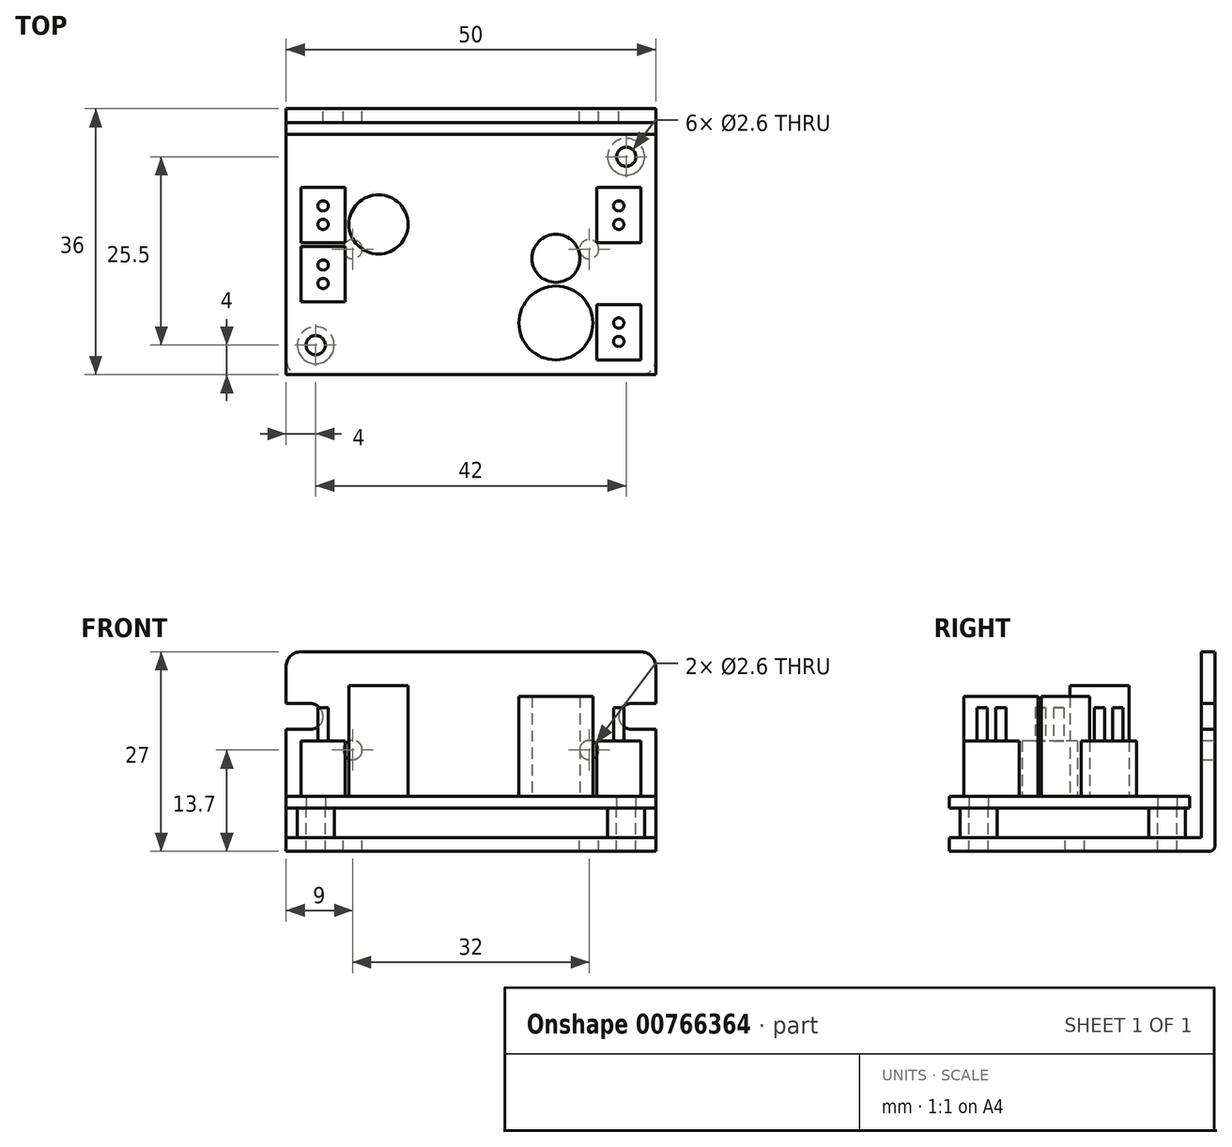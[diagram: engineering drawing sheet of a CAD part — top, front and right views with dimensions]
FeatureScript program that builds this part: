
annotation { "Feature Type Name" : "Feature", "Feature Type Description" : "" }
export const myFeature = defineFeature(function(context is Context, id is Id, definition is map)
    precondition{}
    {
        {
            var Q0;
            Q0=qCreatedBy(makeId("Right.planeOp"),FACE);
            var sketch = newSketch(context, id + "F0", { "sketchPlane" : qUnion([Q0])});
            skLineSegment(sketch, "E0", {"start": v(-17.6, 0) * mm, "end": v(17.6, 0) * mm});
            skLineSegment(sketch, "E1", {"start": v(18.4, 0.8) * mm, "end": v(18.4, 27) * mm});
            skLineSegment(sketch, "E2", {"start": v(18.4, 27) * mm, "end": v(16.55, 27) * mm});
            skLineSegment(sketch, "E3", {"start": v(16.55, 27) * mm, "end": v(16.55, 1.85) * mm});
            skLineSegment(sketch, "E4", {"start": v(16.55, 1.85) * mm, "end": v(-17.6, 1.85) * mm});
            skLineSegment(sketch, "E5", {"start": v(-17.6, 1.85) * mm, "end": v(-17.6, 0) * mm});
            skPoint(sketch, "E6.visualSharp", {"position": v(18.4, 0) * mm});
            skArc(sketch, "E6.filletArc", {"start": v(17.6, 0) * mm, "mid": v(18.17, 0.23) * mm, "end": v(18.4, 0.8) * mm});
            skSolve(sketch);
        }
        {
            var Q0;
            Q0=makeQuery(id+"F0.imprint","IMPRINT",FACE,{"disambiguationData":[TD([[makeQuery(id+"F0.imprint","IMPRINT",EDGE,{"derivedFrom":sQuery(id+"F0.wireOp",EDGE,"E0")}),1.0]])]});
            extrude(context, id + "F1", {"entities" : qUnion([Q0]), "endBound" : BoundingType.SYMMETRIC, "depth" : 50 * mm, "offsetDistance" : 25 * mm});
        }
        {
            var Q0;
            Q0=makeQuery(id+"F1.opExtrude","SWEPT_FACE",FACE,{"disambiguationData":[OSD([sQuery(id+"F0.wireOp",EDGE,"E4")])]});
            var sketch = newSketch(context, id + "F2", { "sketchPlane" : qUnion([Q0])});
            skCircle(sketch, "E7", {"center": v(21, 11.9) * mm, "radius": 1.3 * mm});
            skCircle(sketch, "E8", {"center": v(-21, -13.6) * mm, "radius": 1.3 * mm});
            skCircle(sketch, "E9", {"center": v(-16, -0.6) * mm, "radius": 1.3 * mm});
            skCircle(sketch, "E10", {"center": v(16, -0.6) * mm, "radius": 1.3 * mm});
            skCircle(sketch, "E11", {"center": v(21, 11.9) * mm, "radius": 2.5 * mm});
            skCircle(sketch, "E12", {"center": v(-21, -13.6) * mm, "radius": 2.5 * mm});
            skSolve(sketch);
        }
        {
            var Q0;
            Q0=makeQuery(id+"F2.imprint","IMPRINT",FACE,{"disambiguationData":[TD([[makeQuery(id+"F2.imprint","IMPRINT",EDGE,{"derivedFrom":sQuery(id+"F2.wireOp",EDGE,"E8")}),1.0]])]});
            var Q1;
            Q1=makeQuery(id+"F2.imprint","IMPRINT",FACE,{"disambiguationData":[TD([[makeQuery(id+"F2.imprint","IMPRINT",EDGE,{"derivedFrom":sQuery(id+"F2.wireOp",EDGE,"E9")}),1.0]])]});
            var Q2;
            Q2=makeQuery(id+"F2.imprint","IMPRINT",FACE,{"disambiguationData":[TD([[makeQuery(id+"F2.imprint","IMPRINT",EDGE,{"derivedFrom":sQuery(id+"F2.wireOp",EDGE,"E7")}),1.0]])]});
            var Q3;
            Q3=makeQuery(id+"F2.imprint","IMPRINT",FACE,{"disambiguationData":[TD([[makeQuery(id+"F2.imprint","IMPRINT",EDGE,{"derivedFrom":sQuery(id+"F2.wireOp",EDGE,"E10")}),1.0]])]});
            extrude(context, id + "F3", {"entities" : qUnion([Q0, Q1, Q2, Q3]), "operationType" : NewBodyOperationType.REMOVE, "endBound" : BoundingType.THROUGH_ALL, "oppositeDirection" : true, "depth" : 25 * mm, "offsetDistance" : 25 * mm});
        }
        {
            var Q0;
            Q0=makeQuery(id+"F2.imprint","IMPRINT",FACE,{"disambiguationData":[TD([[makeQuery(id+"F2.imprint","IMPRINT",EDGE,{"derivedFrom":sQuery(id+"F2.wireOp",EDGE,"E8")}),-1.0]])]});
            var Q1;
            Q1=makeQuery(id+"F2.imprint","IMPRINT",FACE,{"disambiguationData":[TD([[makeQuery(id+"F2.imprint","IMPRINT",EDGE,{"derivedFrom":sQuery(id+"F2.wireOp",EDGE,"E7")}),-1.0]])]});
            extrude(context, id + "F4", {"entities" : qUnion([Q0, Q1]), "operationType" : NewBodyOperationType.ADD, "depth" : 4 * mm, "offsetDistance" : 25 * mm});
        }
        {
            var Q0;
            Q0=makeQuery(id+"F1.opExtrude","SWEPT_FACE",FACE,{"disambiguationData":[OSD([sQuery(id+"F0.wireOp",EDGE,"E1")])]});
            var sketch = newSketch(context, id + "F5", { "sketchPlane" : qUnion([Q0])});
            skCircle(sketch, "E13", {"center": v(-16, 13.7) * mm, "radius": 1.3 * mm});
            skCircle(sketch, "E14", {"center": v(16, 13.7) * mm, "radius": 1.3 * mm});
            skCircle(sketch, "E15", {"center": v(-21.75, 18.25) * mm, "radius": 1.75 * mm});
            skCircle(sketch, "E16", {"center": v(21.75, 18.25) * mm, "radius": 1.75 * mm});
            skLineSegment(sketch, "E17", {"start": v(0, 27) * mm, "end": v(0, 0) * mm, "construction": true});
            skLineSegment(sketch, "E18", {"start": v(-21.75, 20) * mm, "end": v(-25, 20) * mm});
            skLineSegment(sketch, "E19", {"start": v(-21.75, 16.5) * mm, "end": v(-25, 16.5) * mm});
            skLineSegment(sketch, "E20.MirrorCS", {"start": v(21.75, 20) * mm, "end": v(25, 20) * mm});
            skLineSegment(sketch, "E21.MirrorCS", {"start": v(21.75, 16.5) * mm, "end": v(25, 16.5) * mm});
            skSolve(sketch);
        }
        {
            var Q0;
            Q0=makeQuery(id+"F5.imprint","IMPRINT",FACE,{"disambiguationData":[TD([[makeQuery(id+"F5.imprint","IMPRINT",EDGE,{"derivedFrom":sQuery(id+"F5.wireOp",EDGE,"E13")}),1.0]])]});
            var Q1;
            Q1=makeQuery(id+"F5.imprint","IMPRINT",FACE,{"disambiguationData":[TD([[makeQuery(id+"F5.imprint","IMPRINT",EDGE,{"derivedFrom":sQuery(id+"F5.wireOp",EDGE,"E14")}),1.0]])]});
            var Q2;
            {var subQ0=sQuery(id+"F5.wireOp",EDGE,"E20.MirrorCS");Q2=makeQuery(id+"F5.imprint","IMPRINT",FACE,{"disambiguationData":[TD([[makeQuery(id+"F5.imprint","IMPRINT",EDGE,{"derivedFrom":subQ0}),-1.0]])]});}
            var Q3;
            {var subQ0=sQuery(id+"F5.wireOp",EDGE,"E16");var subQ1=makeQuery(id+"F5.imprint","INTERSECT",VERTEX,{"derivedFrom":[subQ0,sQuery(id+"F5.wireOp",EDGE,"E20.MirrorCS")]});Q3=makeQuery(id+"F5.imprint","IMPRINT",FACE,{"disambiguationData":[TD([[makeQuery(id+"F5.imprint","IMPRINT",EDGE,{"disambiguationData":[TD([[subQ1,-1.0]])],"derivedFrom":subQ0}),1.0]])]});}
            var Q4;
            {var subQ0=sQuery(id+"F5.wireOp",EDGE,"E18");Q4=makeQuery(id+"F5.imprint","IMPRINT",FACE,{"disambiguationData":[TD([[makeQuery(id+"F5.imprint","IMPRINT",EDGE,{"derivedFrom":subQ0}),1.0]])]});}
            var Q5;
            {var subQ0=sQuery(id+"F5.wireOp",EDGE,"E15");var subQ1=makeQuery(id+"F5.imprint","INTERSECT",VERTEX,{"derivedFrom":[subQ0,sQuery(id+"F5.wireOp",EDGE,"E18")]});Q5=makeQuery(id+"F5.imprint","IMPRINT",FACE,{"disambiguationData":[TD([[makeQuery(id+"F5.imprint","IMPRINT",EDGE,{"disambiguationData":[TD([[subQ1,-1.0]])],"derivedFrom":subQ0}),1.0]])]});}
            extrude(context, id + "F6", {"entities" : qUnion([Q0, Q1, Q2, Q3, Q4, Q5]), "operationType" : NewBodyOperationType.REMOVE, "endBound" : BoundingType.THROUGH_ALL, "oppositeDirection" : true, "depth" : 25 * mm, "offsetDistance" : 25 * mm});
        }
        {
            var Q0;
            Q0=makeQuery(id+"F1.opExtrude","CAP_EDGE",EDGE,{"disambiguationData":[OSD([sQuery(id+"F0.wireOp",EDGE,"E5")])],"isStart":false});
            var Q1;
            Q1=makeQuery(id+"F1.opExtrude","CAP_EDGE",EDGE,{"disambiguationData":[OSD([sQuery(id+"F0.wireOp",EDGE,"E5")])],"isStart":true});
            var Q2;
            Q2=makeQuery(id+"F1.opExtrude","CAP_EDGE",EDGE,{"disambiguationData":[OSD([sQuery(id+"F0.wireOp",EDGE,"E2")])],"isStart":true});
            var Q3;
            Q3=makeQuery(id+"F1.opExtrude","CAP_EDGE",EDGE,{"disambiguationData":[OSD([sQuery(id+"F0.wireOp",EDGE,"E2")])],"isStart":false});
            fillet(context, id + "F7", {"entities" : qUnion([Q0, Q1, Q2, Q3]), "tangentPropagation" : true, "radius" : 2 * mm, "defaultsChanged" : true, "vertexSettings" : [], "allowEdgeOverflow" : false});
        }
        {
            var Q0;
            Q0=makeQuery(id+"F4.opExtrude","CAP_FACE",FACE,{"disambiguationData":[OSD([sQuery(id+"F2.wireOp",EDGE,"E8"),sQuery(id+"F2.wireOp",EDGE,"E12")])],"isStart":false});
            var sketch = newSketch(context, id + "F8", { "sketchPlane" : qUnion([Q0])});
            skLineSegment(sketch, "E22.bottom", {"start": v(-25, -17.6) * mm, "end": v(25, -17.6) * mm});
            skLineSegment(sketch, "E22.top", {"start": v(-25, 14.95) * mm, "end": v(25, 14.95) * mm});
            skLineSegment(sketch, "E22.left", {"start": v(-25, -17.6) * mm, "end": v(-25, 14.95) * mm});
            skLineSegment(sketch, "E22.right", {"start": v(25, -17.6) * mm, "end": v(25, 14.95) * mm});
            skPoint(sketch, "E23.0", {"position": v(-25, 0.47) * mm});
            skPoint(sketch, "E24.0", {"position": v(0, -17.6) * mm});
            skPoint(sketch, "E25.0", {"position": v(25, 0.47) * mm});
            skCircle(sketch, "E26.0", {"center": v(21, 11.9) * mm, "radius": 1.3 * mm});
            skSolve(sketch);
        }
        {
            var Q0;
            Q0=makeQuery(id+"F8.imprint","IMPRINT",FACE,{"disambiguationData":[TD([[makeQuery(id+"F8.imprint","IMPRINT",EDGE,{"derivedFrom":sQuery(id+"F8.wireOp",EDGE,"E22.bottom")}),1.0]])]});
            var Q1;
            Q1=makeQuery(id+"F8.imprint","IMPRINT",FACE,{"disambiguationData":[TD([[makeQuery(id+"F8.imprint","IMPRINT",EDGE,{"derivedFrom":makeQuery(id+"F4.opExtrude","CAP_EDGE",EDGE,{"disambiguationData":[OSD([sQuery(id+"F2.wireOp",EDGE,"E8")])],"isStart":false})}),-1.0]])]});
            extrude(context, id + "F9", {"entities" : qUnion([Q0, Q1]), "depth" : 1.6 * mm, "offsetDistance" : 25 * mm});
        }
        {
            var Q0;
            Q0=makeQuery(id+"F9.opExtrude","CAP_FACE",FACE,{"disambiguationData":[OSD([sQuery(id+"F2.wireOp",EDGE,"E8"),sQuery(id+"F8.wireOp",EDGE,"E22.bottom"),sQuery(id+"F8.wireOp",EDGE,"E22.top"),sQuery(id+"F8.wireOp",EDGE,"E22.left"),sQuery(id+"F8.wireOp",EDGE,"E22.right"),sQuery(id+"F8.wireOp",EDGE,"E26.0")])],"isStart":false});
            var sketch = newSketch(context, id + "F10", { "sketchPlane" : qUnion([Q0])});
            skLineSegment(sketch, "E27.0", {"start": v(-23, 12.95) * mm, "end": v(23, 12.95) * mm, "construction": true});
            skLineSegment(sketch, "E27.1", {"start": v(-23, -15.6) * mm, "end": v(-23, 12.95) * mm, "construction": true});
            skLineSegment(sketch, "E27.2", {"start": v(-23, -15.6) * mm, "end": v(23, -15.6) * mm, "construction": true});
            skLineSegment(sketch, "E27.3", {"start": v(23, -15.6) * mm, "end": v(23, 12.95) * mm, "construction": true});
            skLineSegment(sketch, "E28.bottom", {"start": v(-23, 7.75) * mm, "end": v(-17, 7.75) * mm});
            skLineSegment(sketch, "E28.top", {"start": v(-23, 0.25) * mm, "end": v(-17, 0.25) * mm});
            skLineSegment(sketch, "E28.left", {"start": v(-23, 7.75) * mm, "end": v(-23, 0.25) * mm});
            skLineSegment(sketch, "E28.right", {"start": v(-17, 7.75) * mm, "end": v(-17, 0.25) * mm});
            skLineSegment(sketch, "E29.bottom", {"start": v(-23, -0.25) * mm, "end": v(-17, -0.25) * mm});
            skLineSegment(sketch, "E29.top", {"start": v(-23, -7.75) * mm, "end": v(-17, -7.75) * mm});
            skLineSegment(sketch, "E29.left", {"start": v(-23, -0.25) * mm, "end": v(-23, -7.75) * mm});
            skLineSegment(sketch, "E29.right", {"start": v(-17, -0.25) * mm, "end": v(-17, -7.75) * mm});
            skLineSegment(sketch, "E30.bottom", {"start": v(23, -8.1) * mm, "end": v(17, -8.1) * mm});
            skLineSegment(sketch, "E30.top", {"start": v(23, -15.6) * mm, "end": v(17, -15.6) * mm});
            skLineSegment(sketch, "E30.left", {"start": v(23, -8.1) * mm, "end": v(23, -15.6) * mm});
            skLineSegment(sketch, "E30.right", {"start": v(17, -8.1) * mm, "end": v(17, -15.6) * mm});
            skLineSegment(sketch, "E31.bottom", {"start": v(23, 7.75) * mm, "end": v(17, 7.75) * mm});
            skLineSegment(sketch, "E31.top", {"start": v(23, 0.25) * mm, "end": v(17, 0.25) * mm});
            skLineSegment(sketch, "E31.left", {"start": v(23, 7.75) * mm, "end": v(23, 0.25) * mm});
            skLineSegment(sketch, "E31.right", {"start": v(17, 7.75) * mm, "end": v(17, 0.25) * mm});
            skLineSegment(sketch, "E32", {"start": v(-20, 0.25) * mm, "end": v(-20, -0.25) * mm, "construction": true});
            skPoint(sketch, "E33", {"position": v(-20, 0) * mm});
            skCircle(sketch, "E34", {"center": v(11.5, -10.6) * mm, "radius": 5 * mm});
            skCircle(sketch, "E35", {"center": v(11.5, -1.85) * mm, "radius": 3.25 * mm});
            skCircle(sketch, "E36", {"center": v(-12.5, 2.75) * mm, "radius": 4 * mm});
            skLineSegment(sketch, "E37.bottom", {"start": v(-8, 3.25) * mm, "end": v(1.5, 3.25) * mm});
            skLineSegment(sketch, "E37.top", {"start": v(-8, -1.25) * mm, "end": v(1.5, -1.25) * mm});
            skLineSegment(sketch, "E37.left", {"start": v(-8, 3.25) * mm, "end": v(-8, -1.25) * mm});
            skLineSegment(sketch, "E37.right", {"start": v(1.5, 3.25) * mm, "end": v(1.5, -1.25) * mm});
            skLineSegment(sketch, "E38", {"start": v(-8, -1.25) * mm, "end": v(-17, -1.25) * mm, "construction": true});
            skSolve(sketch);
        }
        {
            var Q0;
            Q0=makeQuery(id+"F10.imprint","IMPRINT",FACE,{"disambiguationData":[TD([[makeQuery(id+"F10.imprint","IMPRINT",EDGE,{"derivedFrom":sQuery(id+"F10.wireOp",EDGE,"E28.bottom")}),-1.0]])]});
            var Q1;
            Q1=makeQuery(id+"F10.imprint","IMPRINT",FACE,{"disambiguationData":[TD([[makeQuery(id+"F10.imprint","IMPRINT",EDGE,{"derivedFrom":sQuery(id+"F10.wireOp",EDGE,"E29.bottom")}),-1.0]])]});
            var Q2;
            Q2=makeQuery(id+"F10.imprint","IMPRINT",FACE,{"disambiguationData":[TD([[makeQuery(id+"F10.imprint","IMPRINT",EDGE,{"derivedFrom":sQuery(id+"F10.wireOp",EDGE,"E30.bottom")}),1.0]])]});
            var Q3;
            Q3=makeQuery(id+"F10.imprint","IMPRINT",FACE,{"disambiguationData":[TD([[makeQuery(id+"F10.imprint","IMPRINT",EDGE,{"derivedFrom":sQuery(id+"F10.wireOp",EDGE,"E31.bottom")}),1.0]])]});
            extrude(context, id + "F11", {"entities" : qUnion([Q0, Q1, Q2, Q3]), "depth" : 7.5 * mm, "offsetDistance" : 25 * mm});
        }
        {
            var Q0;
            Q0=makeQuery(id+"F10.imprint","IMPRINT",FACE,{"disambiguationData":[TD([[makeQuery(id+"F10.imprint","IMPRINT",EDGE,{"derivedFrom":sQuery(id+"F10.wireOp",EDGE,"E34")}),1.0]])]});
            var Q1;
            Q1=makeQuery(id+"F10.imprint","IMPRINT",FACE,{"disambiguationData":[TD([[makeQuery(id+"F10.imprint","IMPRINT",EDGE,{"derivedFrom":sQuery(id+"F10.wireOp",EDGE,"E35")}),1.0]])]});
            extrude(context, id + "F12", {"entities" : qUnion([Q0, Q1]), "depth" : 13.5 * mm, "offsetDistance" : 25 * mm});
        }
        {
            var Q0;
            Q0=makeQuery(id+"F10.imprint","IMPRINT",FACE,{"disambiguationData":[TD([[makeQuery(id+"F10.imprint","IMPRINT",EDGE,{"derivedFrom":sQuery(id+"F10.wireOp",EDGE,"E36")}),1.0]])]});
            extrude(context, id + "F13", {"entities" : qUnion([Q0]), "depth" : 15 * mm, "offsetDistance" : 25 * mm});
        }
        {
            var Q0;
            Q0=makeQuery(id+"F11.opExtrude","CAP_FACE",FACE,{"disambiguationData":[OSD([sQuery(id+"F10.wireOp",EDGE,"E30.bottom"),sQuery(id+"F10.wireOp",EDGE,"E30.top"),sQuery(id+"F10.wireOp",EDGE,"E30.left"),sQuery(id+"F10.wireOp",EDGE,"E30.right")])],"isStart":false});
            var sketch = newSketch(context, id + "F14", { "sketchPlane" : qUnion([Q0])});
            skLineSegment(sketch, "E39", {"start": v(17, -11.85) * mm, "end": v(23, -11.85) * mm, "construction": true});
            skLineSegment(sketch, "E40.0.0", {"start": v(17, 0.25) * mm, "end": v(23, 0.25) * mm, "construction": true});
            skLineSegment(sketch, "E40.0.1", {"start": v(23, 0.25) * mm, "end": v(23, 7.75) * mm, "construction": true});
            skLineSegment(sketch, "E40.0.2", {"start": v(23, 7.75) * mm, "end": v(17, 7.75) * mm, "construction": true});
            skLineSegment(sketch, "E40.0.3", {"start": v(17, 7.75) * mm, "end": v(17, 0.25) * mm, "construction": true});
            skLineSegment(sketch, "E41.0.0", {"start": v(-23, 7.75) * mm, "end": v(-23, 0.25) * mm, "construction": true});
            skLineSegment(sketch, "E41.0.1", {"start": v(-23, 0.25) * mm, "end": v(-17, 0.25) * mm, "construction": true});
            skLineSegment(sketch, "E41.0.2", {"start": v(-17, 0.25) * mm, "end": v(-17, 7.75) * mm, "construction": true});
            skLineSegment(sketch, "E41.0.3", {"start": v(-17, 7.75) * mm, "end": v(-23, 7.75) * mm, "construction": true});
            skLineSegment(sketch, "E42.0.0", {"start": v(-23, -0.25) * mm, "end": v(-23, -7.75) * mm, "construction": true});
            skLineSegment(sketch, "E42.0.1", {"start": v(-23, -7.75) * mm, "end": v(-17, -7.75) * mm, "construction": true});
            skLineSegment(sketch, "E42.0.2", {"start": v(-17, -7.75) * mm, "end": v(-17, -0.25) * mm, "construction": true});
            skLineSegment(sketch, "E42.0.3", {"start": v(-17, -0.25) * mm, "end": v(-23, -0.25) * mm, "construction": true});
            skLineSegment(sketch, "E43", {"start": v(17, 4) * mm, "end": v(23, 4) * mm, "construction": true});
            skLineSegment(sketch, "E44", {"start": v(-23, 4) * mm, "end": v(-17, 4) * mm, "construction": true});
            skLineSegment(sketch, "E45", {"start": v(-23, -4) * mm, "end": v(-17, -4) * mm, "construction": true});
            skCircle(sketch, "E46", {"center": v(20, -13.1) * mm, "radius": 0.7 * mm});
            skPoint(sketch, "E46.centerSnap0", {"position": v(20, -11.85) * mm});
            skCircle(sketch, "E47", {"center": v(20, 2.75) * mm, "radius": 0.7 * mm});
            skPoint(sketch, "E47.centerSnap0", {"position": v(20, 4) * mm});
            skCircle(sketch, "E48", {"center": v(-20, 2.75) * mm, "radius": 0.7 * mm});
            skPoint(sketch, "E48.centerSnap0", {"position": v(-20, 4) * mm});
            skCircle(sketch, "E49", {"center": v(-20, -5.25) * mm, "radius": 0.7 * mm});
            skPoint(sketch, "E49.centerSnap0", {"position": v(-20, -4) * mm});
            skCircle(sketch, "E50.MirrorC", {"center": v(20, -10.6) * mm, "radius": 0.7 * mm});
            skCircle(sketch, "E51.MirrorC", {"center": v(20, 5.25) * mm, "radius": 0.7 * mm});
            skCircle(sketch, "E52.MirrorC", {"center": v(-20, 5.25) * mm, "radius": 0.7 * mm});
            skCircle(sketch, "E53.MirrorC", {"center": v(-20, -2.75) * mm, "radius": 0.7 * mm});
            skLineSegment(sketch, "E54", {"start": v(-20, -5.25) * mm, "end": v(-20, -2.75) * mm, "construction": true});
            skLineSegment(sketch, "E55", {"start": v(-20, 2.75) * mm, "end": v(-20, 5.25) * mm, "construction": true});
            skLineSegment(sketch, "E56", {"start": v(20, 2.75) * mm, "end": v(20, 5.25) * mm, "construction": true});
            skLineSegment(sketch, "E57", {"start": v(20, -13.1) * mm, "end": v(20, -10.6) * mm, "construction": true});
            skSolve(sketch);
        }
        {
            var Q0;
            Q0 = qSketchRegion(id + "F14", true);
            extrude(context, id + "F15", {"entities" : qUnion([Q0]), "depth" : 4.5 * mm, "offsetDistance" : 25 * mm});
        }
    });
